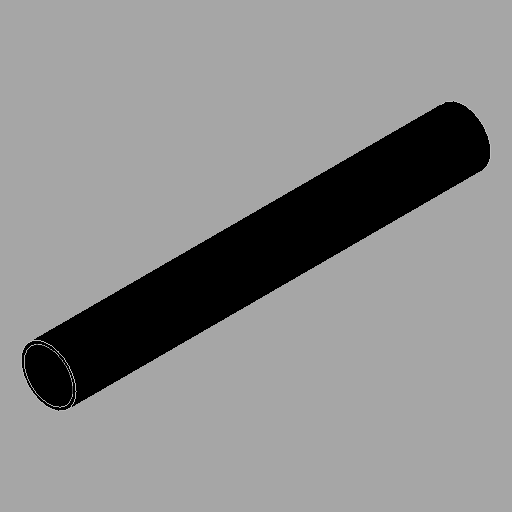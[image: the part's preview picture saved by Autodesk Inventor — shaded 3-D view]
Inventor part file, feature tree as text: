
AUTODESK INVENTOR PART (.ipt)
format: ipt  version: 2025 (Build 290162000, 162)  size: 82,432 bytes
history: native  units: in
note: dims shown in document units (in); Inventor stores cm internally (conversion verified against a paired STEP export)
features: extrude x1, sketch x1
ambient origin geometry x8: Origin, YZ Plane, XZ Plane, XY Plane, X Axis, Y Axis, Z Axis, Center Point
bodies: Solid1 (feature_tree)
feature tree (2):
  extrude  "Extrusion1"  Depth=8.5in
  sketch  "Sketch1"  dims[d0=1.125in d1=1.0in d2=8.5in d3=0.0in]
